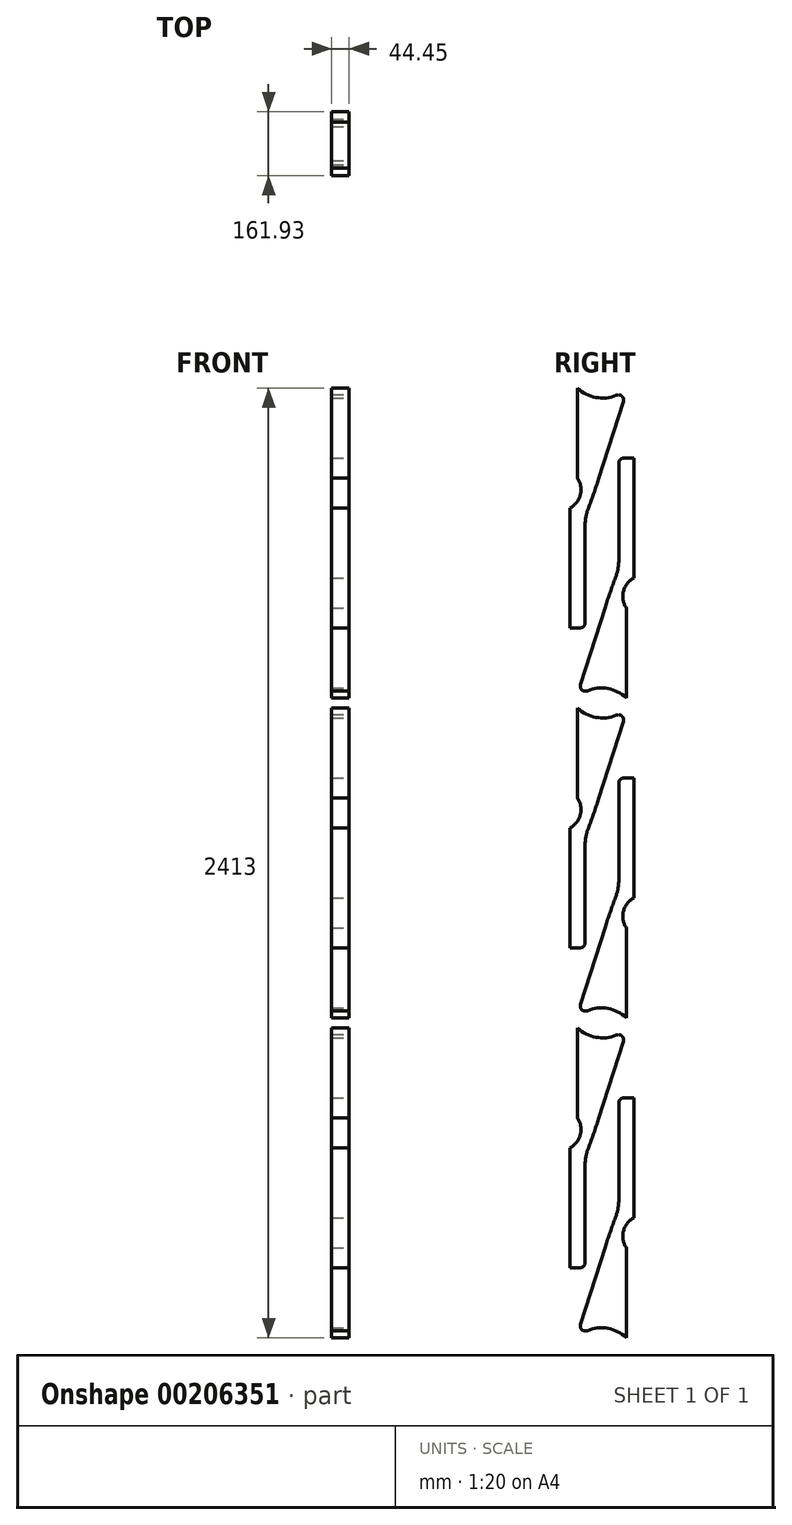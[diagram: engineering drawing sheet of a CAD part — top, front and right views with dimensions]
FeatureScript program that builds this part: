
annotation { "Feature Type Name" : "Feature", "Feature Type Description" : "" }
export const myFeature = defineFeature(function(context is Context, id is Id, definition is map)
    precondition{}
    {
        {
            var Q0;
            Q0=qCreatedBy(makeId("Top.planeOp"),FACE);
            var sketch = newSketch(context, id + "F0", { "sketchPlane" : qUnion([Q0])});
            skLineSegment(sketch, "E0.bottom", {"start": v(0, 0) * mm, "end": v(44.45, 0) * mm});
            skLineSegment(sketch, "E0.top", {"start": v(0, 184.15) * mm, "end": v(44.45, 184.15) * mm});
            skLineSegment(sketch, "E0.left", {"start": v(0, 0) * mm, "end": v(0, 184.15) * mm});
            skLineSegment(sketch, "E0.right", {"start": v(44.45, 0) * mm, "end": v(44.45, 184.15) * mm});
            skSolve(sketch);
        }
        {
            var Q0;
            Q0 = qSketchRegion(id + "F0", true);
            extrude(context, id + "F1", {"entities" : qUnion([Q0]), "depth" : 2438.4 * mm});
        }
        {
            var Q0;
            Q0=makeQuery(id+"F1.opExtrude","SWEPT_FACE",FACE,{"disambiguationData":[OSD([sQuery(id+"F0.wireOp",EDGE,"E0.right")])]});
            var sketch = newSketch(context, id + "F2", { "sketchPlane" : qUnion([Q0])});
            skLineSegment(sketch, "E1", {"start": v(12.7, 1816.1) * mm, "end": v(12.7, 2120.9) * mm});
            skLineSegment(sketch, "E2", {"start": v(12.7, 1816.1) * mm, "end": v(38.1, 1816.1) * mm});
            skArc(sketch, "E3", {"start": v(38.1, 1816.1) * mm, "mid": v(47.08, 1819.82) * mm, "end": v(50.8, 1828.8) * mm});
            skLineSegment(sketch, "E4", {"start": v(50.8, 1828.8) * mm, "end": v(50.8, 2074.71) * mm});
            skArc(sketch, "E5", {"start": v(50.8, 2074.71) * mm, "mid": v(52.86, 2097.5) * mm, "end": v(58.98, 2119.55) * mm});
            skLineSegment(sketch, "E6", {"start": v(85.11, 2194.7) * mm, "end": v(148, 2391.95) * mm});
            skArc(sketch, "E7", {"start": v(12.7, 2120.9) * mm, "mid": v(38.96, 2154.82) * mm, "end": v(31.75, 2197.1) * mm});
            skLineSegment(sketch, "E8", {"start": v(31.75, 2197.1) * mm, "end": v(31.75, 2425.7) * mm});
            skArc(sketch, "E9", {"start": v(31.75, 2425.7) * mm, "mid": v(78.64, 2401.8) * mm, "end": v(130.96, 2407.5) * mm});
            skLineSegment(sketch, "E10", {"start": v(158.75, 2425.7) * mm, "end": v(31.75, 2425.7) * mm, "construction": true});
            skLineSegment(sketch, "E11", {"start": v(95.25, 2425.7) * mm, "end": v(95.25, 2400.3) * mm, "construction": true});
            skArc(sketch, "E12", {"start": v(148, 2391.95) * mm, "mid": v(144.46, 2405.18) * mm, "end": v(130.96, 2407.5) * mm});
            skArc(sketch, "E13", {"start": v(130.96, 2407.5) * mm, "mid": v(145.68, 2415.34) * mm, "end": v(158.75, 2425.7) * mm, "construction": true});
            skArc(sketch, "E14", {"start": v(58.98, 2119.55) * mm, "mid": v(72.54, 2156.95) * mm, "end": v(85.11, 2194.7) * mm});
            skLineSegment(sketch, "E15", {"start": v(184.15, 1625.6) * mm, "end": v(0, 1625.6) * mm, "construction": true});
            skLineSegment(sketch, "E16", {"start": v(92.08, 2438.4) * mm, "end": v(95.25, 0) * mm, "construction": true});
            skPoint(sketch, "E16.endSnap0", {"position": v(95.25, 2413) * mm});
            skLineSegment(sketch, "E17", {"start": v(184.15, 1219.2) * mm, "end": v(0, 1219.2) * mm, "construction": true});
            skLineSegment(sketch, "E18", {"start": v(184.15, 609.6) * mm, "end": v(0, 609.6) * mm, "construction": true});
            skLineSegment(sketch, "E19", {"start": v(184.15, 1828.8) * mm, "end": v(0, 1828.8) * mm, "construction": true});
            skLineSegment(sketch, "E20", {"start": v(184.15, 812.8) * mm, "end": v(0, 812.8) * mm, "construction": true});
            skLineSegment(sketch, "E21.0.1.0", {"start": v(50.8, 1016) * mm, "end": v(50.8, 1261.91) * mm});
            skLineSegment(sketch, "E21.0.1.1", {"start": v(12.7, 1003.3) * mm, "end": v(12.7, 1308.1) * mm});
            skArc(sketch, "E21.0.1.2", {"start": v(58.98, 1306.75) * mm, "mid": v(72.54, 1344.15) * mm, "end": v(85.11, 1381.9) * mm});
            skLineSegment(sketch, "E21.0.1.3", {"start": v(85.11, 1381.9) * mm, "end": v(148, 1579.15) * mm});
            skLineSegment(sketch, "E21.0.1.4", {"start": v(31.75, 1384.3) * mm, "end": v(31.75, 1612.9) * mm});
            skArc(sketch, "E21.0.1.5", {"start": v(31.75, 1612.9) * mm, "mid": v(78.64, 1589) * mm, "end": v(130.96, 1594.7) * mm});
            skLineSegment(sketch, "E21.0.1.6", {"start": v(184.15, 1016) * mm, "end": v(0, 1016) * mm, "construction": true});
            skPoint(sketch, "E21.0.1.7", {"position": v(95.25, 1600.2) * mm});
            skArc(sketch, "E21.0.1.8", {"start": v(12.7, 1308.1) * mm, "mid": v(38.96, 1342.02) * mm, "end": v(31.75, 1384.3) * mm});
            skLineSegment(sketch, "E21.0.1.9", {"start": v(158.75, 1612.9) * mm, "end": v(31.75, 1612.9) * mm, "construction": true});
            skLineSegment(sketch, "E21.0.1.10", {"start": v(12.7, 1003.3) * mm, "end": v(38.1, 1003.3) * mm});
            skLineSegment(sketch, "E21.0.1.11", {"start": v(95.25, 1612.9) * mm, "end": v(95.25, 1587.5) * mm, "construction": true});
            skArc(sketch, "E21.0.1.12", {"start": v(50.8, 1261.91) * mm, "mid": v(52.86, 1284.7) * mm, "end": v(58.98, 1306.75) * mm});
            skArc(sketch, "E21.0.1.13", {"start": v(130.96, 1594.7) * mm, "mid": v(145.68, 1602.54) * mm, "end": v(158.75, 1612.9) * mm, "construction": true});
            skArc(sketch, "E21.0.1.14", {"start": v(38.1, 1003.3) * mm, "mid": v(47.08, 1007.02) * mm, "end": v(50.8, 1016) * mm});
            skArc(sketch, "E21.0.1.15", {"start": v(148, 1579.15) * mm, "mid": v(144.46, 1592.38) * mm, "end": v(130.96, 1594.7) * mm});
            skLineSegment(sketch, "E21.direction1", {"start": v(-1366.9, 2657.56) * mm, "end": v(-1341.5, 2657.56) * mm, "construction": true});
            skLineSegment(sketch, "E21.direction2", {"start": v(-1366.9, 2657.56) * mm, "end": v(-1366.9, 1844.76) * mm, "construction": true});
            skPoint(sketch, "E22", {"position": v(93.66, 1219.2) * mm});
            skLineSegment(sketch, "E23.0.0.2", {"start": v(50.8, 203.2) * mm, "end": v(50.8, 449.11) * mm});
            skLineSegment(sketch, "E23.3.0.2", {"start": v(12.7, 190.5) * mm, "end": v(12.7, 495.3) * mm});
            skArc(sketch, "E23.6.0.2", {"start": v(58.98, 493.95) * mm, "mid": v(72.54, 531.35) * mm, "end": v(85.11, 569.1) * mm});
            skLineSegment(sketch, "E23.10.0.2", {"start": v(85.11, 569.1) * mm, "end": v(148, 766.35) * mm});
            skLineSegment(sketch, "E23.13.0.2", {"start": v(31.75, 571.5) * mm, "end": v(31.75, 800.1) * mm});
            skArc(sketch, "E23.16.0.2", {"start": v(31.75, 800.1) * mm, "mid": v(78.64, 776.2) * mm, "end": v(130.96, 781.9) * mm});
            skLineSegment(sketch, "E23.20.0.2", {"start": v(184.15, 203.2) * mm, "end": v(0, 203.2) * mm, "construction": true});
            skPoint(sketch, "E23.23.0.2", {"position": v(95.25, 787.4) * mm});
            skArc(sketch, "E23.24.0.2", {"start": v(12.7, 495.3) * mm, "mid": v(38.96, 529.22) * mm, "end": v(31.75, 571.5) * mm});
            skLineSegment(sketch, "E23.28.0.2", {"start": v(158.75, 800.1) * mm, "end": v(31.75, 800.1) * mm, "construction": true});
            skLineSegment(sketch, "E23.31.0.2", {"start": v(12.7, 190.5) * mm, "end": v(38.1, 190.5) * mm});
            skLineSegment(sketch, "E23.34.0.2", {"start": v(95.25, 800.1) * mm, "end": v(95.25, 774.7) * mm, "construction": true});
            skArc(sketch, "E23.37.0.2", {"start": v(50.8, 449.11) * mm, "mid": v(52.86, 471.9) * mm, "end": v(58.98, 493.95) * mm});
            skArc(sketch, "E23.41.0.2", {"start": v(130.96, 781.9) * mm, "mid": v(145.68, 789.74) * mm, "end": v(158.75, 800.1) * mm, "construction": true});
            skArc(sketch, "E23.45.0.2", {"start": v(38.1, 190.5) * mm, "mid": v(47.08, 194.22) * mm, "end": v(50.8, 203.2) * mm});
            skArc(sketch, "E23.49.0.2", {"start": v(148, 766.35) * mm, "mid": v(144.46, 779.58) * mm, "end": v(130.96, 781.9) * mm});
            skLineSegment(sketch, "E24.1.0", {"start": v(136.53, 1422.4) * mm, "end": v(136.53, 1176.49) * mm});
            skLineSegment(sketch, "E24.1.1", {"start": v(3.17, 1422.4) * mm, "end": v(187.33, 1422.4) * mm, "construction": true});
            skArc(sketch, "E24.1.2", {"start": v(128.35, 1131.65) * mm, "mid": v(114.79, 1094.25) * mm, "end": v(102.21, 1056.5) * mm});
            skLineSegment(sketch, "E24.1.3", {"start": v(102.21, 1056.5) * mm, "end": v(39.33, 859.25) * mm});
            skArc(sketch, "E24.1.4", {"start": v(174.62, 1130.3) * mm, "mid": v(148.37, 1096.38) * mm, "end": v(155.58, 1054.1) * mm});
            skArc(sketch, "E24.1.5", {"start": v(136.52, 1176.49) * mm, "mid": v(134.46, 1153.7) * mm, "end": v(128.35, 1131.65) * mm});
            skLineSegment(sketch, "E24.1.6", {"start": v(174.63, 1435.1) * mm, "end": v(174.63, 1130.3) * mm});
            skLineSegment(sketch, "E24.1.7", {"start": v(3.17, 812.8) * mm, "end": v(187.32, 812.8) * mm, "construction": true});
            skLineSegment(sketch, "E24.1.8", {"start": v(28.57, 825.5) * mm, "end": v(155.58, 825.5) * mm, "construction": true});
            skArc(sketch, "E24.1.9", {"start": v(155.57, 825.5) * mm, "mid": v(108.68, 849.4) * mm, "end": v(56.36, 843.7) * mm});
            skPoint(sketch, "E24.1.10", {"position": v(92.08, 838.2) * mm});
            skLineSegment(sketch, "E24.1.11", {"start": v(155.58, 1054.1) * mm, "end": v(155.58, 825.5) * mm});
            skLineSegment(sketch, "E24.1.13", {"start": v(3.17, 1219.2) * mm, "end": v(187.33, 1219.2) * mm, "construction": true});
            skLineSegment(sketch, "E24.1.14", {"start": v(92.08, 825.5) * mm, "end": v(92.08, 850.9) * mm, "construction": true});
            skArc(sketch, "E24.1.15", {"start": v(39.33, 859.25) * mm, "mid": v(42.87, 846.02) * mm, "end": v(56.36, 843.7) * mm});
            skLineSegment(sketch, "E24.1.16", {"start": v(174.62, 1435.1) * mm, "end": v(149.22, 1435.1) * mm});
            skArc(sketch, "E24.1.17", {"start": v(56.36, 843.7) * mm, "mid": v(41.64, 835.86) * mm, "end": v(28.58, 825.5) * mm, "construction": true});
            skArc(sketch, "E24.1.18", {"start": v(149.22, 1435.1) * mm, "mid": v(140.24, 1431.38) * mm, "end": v(136.52, 1422.4) * mm});
            skLineSegment(sketch, "E25.0.1.0", {"start": v(174.62, 2247.9) * mm, "end": v(149.22, 2247.9) * mm});
            skArc(sketch, "E25.0.1.1", {"start": v(136.52, 1989.29) * mm, "mid": v(134.46, 1966.5) * mm, "end": v(128.35, 1944.45) * mm});
            skLineSegment(sketch, "E25.0.1.2", {"start": v(174.63, 2247.9) * mm, "end": v(174.63, 1943.1) * mm});
            skLineSegment(sketch, "E25.0.1.3", {"start": v(136.53, 2235.2) * mm, "end": v(136.53, 1989.29) * mm});
            skArc(sketch, "E25.0.1.4", {"start": v(149.22, 2247.9) * mm, "mid": v(140.24, 2244.18) * mm, "end": v(136.52, 2235.2) * mm});
            skArc(sketch, "E25.0.1.5", {"start": v(174.62, 1943.1) * mm, "mid": v(148.37, 1909.18) * mm, "end": v(155.58, 1866.9) * mm});
            skLineSegment(sketch, "E25.0.1.6", {"start": v(102.21, 1869.3) * mm, "end": v(39.33, 1672.05) * mm});
            skArc(sketch, "E25.0.1.7", {"start": v(128.35, 1944.45) * mm, "mid": v(114.79, 1907.05) * mm, "end": v(102.21, 1869.3) * mm});
            skLineSegment(sketch, "E25.0.1.8", {"start": v(155.58, 1866.9) * mm, "end": v(155.58, 1638.3) * mm});
            skArc(sketch, "E25.0.1.9", {"start": v(155.57, 1638.3) * mm, "mid": v(108.68, 1662.2) * mm, "end": v(56.36, 1656.5) * mm});
            skArc(sketch, "E25.0.1.10", {"start": v(39.33, 1672.05) * mm, "mid": v(42.87, 1658.82) * mm, "end": v(56.36, 1656.5) * mm});
            skArc(sketch, "E25.0.1.11", {"start": v(56.36, 1656.5) * mm, "mid": v(41.64, 1648.66) * mm, "end": v(28.58, 1638.3) * mm, "construction": true});
            skLineSegment(sketch, "E25.0.1.12", {"start": v(28.57, 1638.3) * mm, "end": v(155.58, 1638.3) * mm, "construction": true});
            skLineSegment(sketch, "E25.direction1", {"start": v(0, 758.82) * mm, "end": v(92.07, 758.82) * mm, "construction": true});
            skLineSegment(sketch, "E25.direction2", {"start": v(92.07, 758.82) * mm, "end": v(92.07, 1571.62) * mm, "construction": true});
            skLineSegment(sketch, "E26.0.1.0", {"start": v(174.63, 622.3) * mm, "end": v(174.63, 317.5) * mm});
            skLineSegment(sketch, "E26.0.1.1", {"start": v(174.62, 622.3) * mm, "end": v(149.22, 622.3) * mm});
            skArc(sketch, "E26.0.1.2", {"start": v(149.22, 622.3) * mm, "mid": v(140.24, 618.58) * mm, "end": v(136.52, 609.6) * mm});
            skLineSegment(sketch, "E26.0.1.3", {"start": v(136.53, 609.6) * mm, "end": v(136.53, 363.69) * mm});
            skArc(sketch, "E26.0.1.4", {"start": v(136.52, 363.69) * mm, "mid": v(134.46, 340.9) * mm, "end": v(128.35, 318.85) * mm});
            skArc(sketch, "E26.0.1.5", {"start": v(174.62, 317.5) * mm, "mid": v(148.37, 283.58) * mm, "end": v(155.58, 241.3) * mm});
            skLineSegment(sketch, "E26.0.1.6", {"start": v(155.58, 241.3) * mm, "end": v(155.58, 12.7) * mm});
            skArc(sketch, "E26.0.1.7", {"start": v(155.57, 12.7) * mm, "mid": v(108.68, 36.6) * mm, "end": v(56.36, 30.9) * mm});
            skArc(sketch, "E26.0.1.8", {"start": v(39.33, 46.45) * mm, "mid": v(42.87, 33.22) * mm, "end": v(56.36, 30.9) * mm});
            skLineSegment(sketch, "E26.0.1.9", {"start": v(102.21, 243.7) * mm, "end": v(39.33, 46.45) * mm});
            skArc(sketch, "E26.0.1.10", {"start": v(128.35, 318.85) * mm, "mid": v(114.79, 281.45) * mm, "end": v(102.21, 243.7) * mm});
            skLineSegment(sketch, "E26.direction1", {"start": v(174.63, 1130.3) * mm, "end": v(184.15, 1130.3) * mm, "construction": true});
            skLineSegment(sketch, "E26.direction2", {"start": v(174.63, 1130.3) * mm, "end": v(174.63, 317.5) * mm, "construction": true});
            skSolve(sketch);
        }
        {
            var Q0;
            Q0=makeQuery(id+"F2.imprint","IMPRINT",FACE,{"disambiguationData":[TD([[makeQuery(id+"F2.imprint","IMPRINT",EDGE,{"derivedFrom":sQuery(id+"F2.wireOp",EDGE,"E1")}),1.0]])]});
            extrude(context, id + "F3", {"entities" : qUnion([Q0]), "operationType" : NewBodyOperationType.REMOVE, "endBound" : BoundingType.THROUGH_ALL, "oppositeDirection" : true, "depth" : 25.4 * mm});
        }
    });
